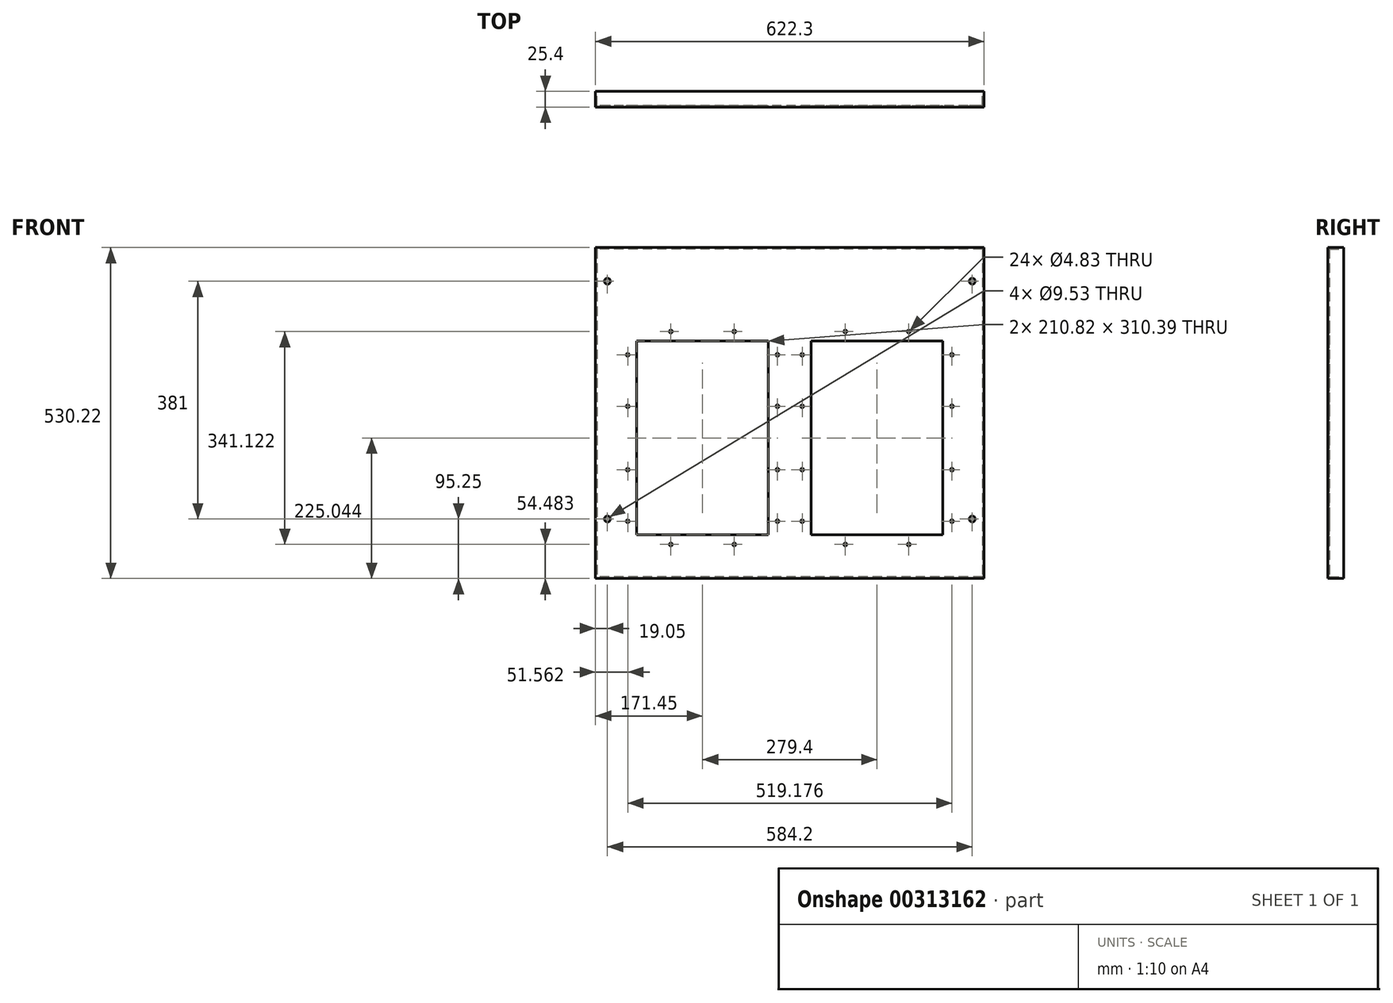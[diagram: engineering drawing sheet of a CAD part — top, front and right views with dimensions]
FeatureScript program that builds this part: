
annotation { "Feature Type Name" : "Feature", "Feature Type Description" : "" }
export const myFeature = defineFeature(function(context is Context, id is Id, definition is map)
    precondition{}
    {
        {
            var Q0;
            Q0=qCreatedBy(makeId("Front.planeOp"),FACE);
            var sketch = newSketch(context, id + "F0", { "sketchPlane" : qUnion([Q0])});
            skLineSegment(sketch, "E0.bottom", {"start": v(311.15, 530.22) * mm, "end": v(-311.15, 530.22) * mm});
            skLineSegment(sketch, "E0.top", {"start": v(311.15, 0) * mm, "end": v(-311.15, 0) * mm});
            skLineSegment(sketch, "E0.left", {"start": v(311.15, 530.22) * mm, "end": v(311.15, 0) * mm});
            skLineSegment(sketch, "E0.right", {"start": v(-311.15, 530.22) * mm, "end": v(-311.15, 0) * mm});
            skLineSegment(sketch, "E1.bottom", {"start": v(-34.29, 380.24) * mm, "end": v(-245.1, 380.24) * mm});
            skLineSegment(sketch, "E1.top", {"start": v(-34.29, 69.85) * mm, "end": v(-245.1, 69.85) * mm});
            skLineSegment(sketch, "E1.left", {"start": v(-34.29, 380.24) * mm, "end": v(-34.29, 69.85) * mm});
            skLineSegment(sketch, "E1.right", {"start": v(-245.1, 380.24) * mm, "end": v(-245.1, 69.85) * mm});
            skPoint(sketch, "E1.middle", {"position": v(-139.7, 225.04) * mm});
            skCircle(sketch, "E2", {"center": v(-190.5, 395.6) * mm, "radius": 2.41 * mm});
            skCircle(sketch, "E3", {"center": v(-88.9, 395.6) * mm, "radius": 2.41 * mm});
            skCircle(sketch, "E4", {"center": v(-19.81, 358.4) * mm, "radius": 2.41 * mm});
            skCircle(sketch, "E5", {"center": v(-19.81, 275.84) * mm, "radius": 2.41 * mm});
            skCircle(sketch, "E6", {"center": v(-19.81, 174.24) * mm, "radius": 2.41 * mm});
            skCircle(sketch, "E7", {"center": v(-19.81, 91.7) * mm, "radius": 2.41 * mm});
            skCircle(sketch, "E8", {"center": v(-190.5, 54.48) * mm, "radius": 2.41 * mm});
            skCircle(sketch, "E9", {"center": v(-88.9, 54.48) * mm, "radius": 2.41 * mm});
            skCircle(sketch, "E10", {"center": v(-259.59, 91.7) * mm, "radius": 2.41 * mm});
            skCircle(sketch, "E11", {"center": v(-259.59, 174.24) * mm, "radius": 2.41 * mm});
            skCircle(sketch, "E12", {"center": v(-259.59, 275.84) * mm, "radius": 2.41 * mm});
            skCircle(sketch, "E13", {"center": v(-259.59, 358.4) * mm, "radius": 2.41 * mm});
            skPoint(sketch, "E14.1.0.0", {"position": v(139.7, 225.04) * mm});
            skLineSegment(sketch, "E14.1.0.1", {"start": v(245.11, 380.24) * mm, "end": v(245.11, 69.85) * mm});
            skLineSegment(sketch, "E14.1.0.2", {"start": v(34.3, 380.24) * mm, "end": v(34.3, 69.85) * mm});
            skLineSegment(sketch, "E14.1.0.3", {"start": v(245.11, 69.85) * mm, "end": v(34.3, 69.85) * mm});
            skLineSegment(sketch, "E14.1.0.4", {"start": v(245.11, 380.24) * mm, "end": v(34.3, 380.24) * mm});
            skCircle(sketch, "E14.1.0.5", {"center": v(259.59, 91.7) * mm, "radius": 2.41 * mm});
            skCircle(sketch, "E14.1.0.6", {"center": v(19.81, 174.24) * mm, "radius": 2.41 * mm});
            skCircle(sketch, "E14.1.0.7", {"center": v(259.59, 275.84) * mm, "radius": 2.41 * mm});
            skCircle(sketch, "E14.1.0.8", {"center": v(88.9, 54.48) * mm, "radius": 2.41 * mm});
            skCircle(sketch, "E14.1.0.9", {"center": v(259.59, 358.4) * mm, "radius": 2.41 * mm});
            skCircle(sketch, "E14.1.0.10", {"center": v(190.5, 54.48) * mm, "radius": 2.41 * mm});
            skCircle(sketch, "E14.1.0.11", {"center": v(88.9, 395.6) * mm, "radius": 2.41 * mm});
            skCircle(sketch, "E14.1.0.12", {"center": v(190.5, 395.6) * mm, "radius": 2.41 * mm});
            skCircle(sketch, "E14.1.0.13", {"center": v(259.59, 174.24) * mm, "radius": 2.41 * mm});
            skCircle(sketch, "E14.1.0.14", {"center": v(19.81, 358.4) * mm, "radius": 2.41 * mm});
            skCircle(sketch, "E14.1.0.15", {"center": v(19.81, 275.84) * mm, "radius": 2.41 * mm});
            skCircle(sketch, "E14.1.0.16", {"center": v(19.81, 91.7) * mm, "radius": 2.41 * mm});
            skLineSegment(sketch, "E14.direction1", {"start": v(-245.1, 69.85) * mm, "end": v(34.3, 69.85) * mm, "construction": true});
            skCircle(sketch, "E15", {"center": v(292.1, 476.25) * mm, "radius": 4.76 * mm});
            skCircle(sketch, "E16", {"center": v(292.1, 95.25) * mm, "radius": 4.76 * mm});
            skCircle(sketch, "E17", {"center": v(-292.1, 95.25) * mm, "radius": 4.76 * mm});
            skCircle(sketch, "E18", {"center": v(-292.1, 476.25) * mm, "radius": 4.76 * mm});
            skSolve(sketch);
        }
        {
            var Q0;
            Q0 = qSketchRegion(id + "F0", true);
            extrude(context, id + "F1", {"entities" : qUnion([Q0]), "depth" : 25.4 * mm});
        }
        {
            var Q0;
            Q0=makeQuery(id+"F1.opExtrude","CAP_FACE",FACE,{"disambiguationData":[OSD([sQuery(id+"F0.wireOp",EDGE,"E0.bottom"),sQuery(id+"F0.wireOp",EDGE,"E0.top"),sQuery(id+"F0.wireOp",EDGE,"E0.left"),sQuery(id+"F0.wireOp",EDGE,"E0.right"),sQuery(id+"F0.wireOp",EDGE,"E1.bottom"),sQuery(id+"F0.wireOp",EDGE,"E1.top"),sQuery(id+"F0.wireOp",EDGE,"E1.left"),sQuery(id+"F0.wireOp",EDGE,"E1.right"),sQuery(id+"F0.wireOp",EDGE,"E2"),sQuery(id+"F0.wireOp",EDGE,"E3"),sQuery(id+"F0.wireOp",EDGE,"E4"),sQuery(id+"F0.wireOp",EDGE,"E5"),sQuery(id+"F0.wireOp",EDGE,"E6"),sQuery(id+"F0.wireOp",EDGE,"E7"),sQuery(id+"F0.wireOp",EDGE,"E8"),sQuery(id+"F0.wireOp",EDGE,"E9"),sQuery(id+"F0.wireOp",EDGE,"E10"),sQuery(id+"F0.wireOp",EDGE,"E11"),sQuery(id+"F0.wireOp",EDGE,"E12"),sQuery(id+"F0.wireOp",EDGE,"E13"),sQuery(id+"F0.wireOp",EDGE,"E14.1.0.1"),sQuery(id+"F0.wireOp",EDGE,"E14.1.0.2"),sQuery(id+"F0.wireOp",EDGE,"E14.1.0.3"),sQuery(id+"F0.wireOp",EDGE,"E14.1.0.4"),sQuery(id+"F0.wireOp",EDGE,"E14.1.0.5"),sQuery(id+"F0.wireOp",EDGE,"E14.1.0.6"),sQuery(id+"F0.wireOp",EDGE,"E14.1.0.7"),sQuery(id+"F0.wireOp",EDGE,"E14.1.0.8"),sQuery(id+"F0.wireOp",EDGE,"E14.1.0.9"),sQuery(id+"F0.wireOp",EDGE,"E14.1.0.10"),sQuery(id+"F0.wireOp",EDGE,"E14.1.0.11"),sQuery(id+"F0.wireOp",EDGE,"E14.1.0.12"),sQuery(id+"F0.wireOp",EDGE,"E14.1.0.13"),sQuery(id+"F0.wireOp",EDGE,"E14.1.0.14"),sQuery(id+"F0.wireOp",EDGE,"E14.1.0.15"),sQuery(id+"F0.wireOp",EDGE,"E14.1.0.16")])],"isStart":true});
            shell(context, id + "F2", {"entities" : qUnion([Q0]), "thickness" : 2.54 * mm});
        }
        {
            var Q0;
            Q0=makeQuery(id+"F2.opShell","OFFSET_FACE",FACE,{"disambiguationData":[OSD([sQuery(id+"F0.wireOp",EDGE,"E0.bottom")])]});
            var sketch = newSketch(context, id + "F3", { "sketchPlane" : qUnion([Q0])});
            skLineSegment(sketch, "E19.bottom", {"start": v(-308.6, 22.86) * mm, "end": v(308.61, 22.86) * mm});
            skLineSegment(sketch, "E19.top", {"start": v(-308.6, 0) * mm, "end": v(308.61, 0) * mm});
            skLineSegment(sketch, "E19.left", {"start": v(-308.6, 22.86) * mm, "end": v(-308.6, 0) * mm});
            skLineSegment(sketch, "E19.right", {"start": v(308.61, 22.86) * mm, "end": v(308.61, 0) * mm});
            skSolve(sketch);
        }
        {
            var Q0;
            Q0 = qSketchRegion(id + "F3", true);
            var Q1;
            Q1=makeQuery(id+"F2.opShell","OFFSET_FACE",FACE,{"disambiguationData":[OSD([sQuery(id+"F0.wireOp",EDGE,"E0.top")])]});
            extrude(context, id + "F4", {"entities" : qUnion([Q0]), "operationType" : NewBodyOperationType.REMOVE, "endBound" : BoundingType.UP_TO_SURFACE, "endBoundEntityFace" : qUnion([Q1]), "depth" : 25.4 * mm});
        }
    });
